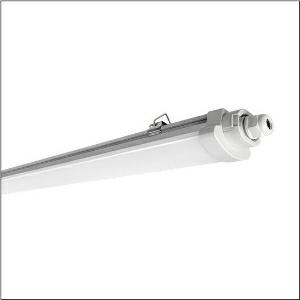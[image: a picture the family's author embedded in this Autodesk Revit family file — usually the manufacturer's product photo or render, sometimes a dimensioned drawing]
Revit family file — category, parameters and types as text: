
# Revit family: monsun_r__41_51fk20mn460a003_94ec
name_source: partatom
category: Lighting Fixtures
units: mm (PartAtom-declared; Revit-internal decimal feet)

## family parameters
Cut with Voids When Loaded = No
Host = Face
Light Source = No
Part Type = Normal
Room Calculation Point = No
Round Connector Dimension = Use Diameter
Shared = No

## types (1)
- --- (1 x LED, 6000 lm, 46 W, 4000K)
    Apparent Load = 46 VA
    CIE Flux Codes = 44 74 91 91 100
    Color Rendering = 80
    Color Temperature = 4000K
    Default Elevation = 1800 mm
    Description = Monsun® 41, damp-proof luminaire, primary optical cover: diffuser, of PC, frosted, light emission: direct distribution, primary light characteristic: symmetric, installation type: suspended mounting, surface-mounted, LED, rated luminous flux: 6.000lm, luminous efficacy: 130lm/W, light colour: 840, colour temperature: 4000K, control gear: ON/OFF Multilumen, with terminal, 3-pole, through-wiring: 3x 1.5mm², mains connection: 220..240V, AC, 50/60Hz, rated input power: 46W, housing, luminaire housing, of PC, grey, length: 1.500mm, width: 79mm, height: 52mm, end cap, of PC, grey, ceiling mounting element, of stainless steel (V2A), protection rating (complete): IP65, insulation class (complete): insulation class II (safety insulation), certification: CE, UKCA, protection symbol: D, impact resistance: IK08, permissible operating ambient temperature: -20..+35°C, corresponds to IFS (International Featured Standards) requirements for safety and quality in the food industry, contact your sales advisor before using the luminaires in applications with unclear chemical exposure, large temperature fluctuations or condensation-forming humidity, packaging unit: 1 piece
    Height = 54 mm
    Lamp = 1 x LED
    Lamp Light Flux = 6000 lm
    Lamp Power = 46 W
    Lamp count = 1
    Length = 1500 mm
    Luminous efficacy = 130 lm/W
    Manufacturer = Siteco
    ModVariant = No
    Model = 51FK20MN460A003
    Mounting Place = Ceiling
    Mounting Type = Surface mounted
    Number of Poles = 1
    OnlyDefault = Yes
    Power Factor = 1
    Product Name = Monsun® 41
    Product group = damp-proof luminaire
    ProductGroupID = 300
    Protection Class = Protection class II
    Protection Degree = IP 65
    RLX_Detail_Level = 1
    RLX_Emergency_Light_Flux = 0 lm
    RLX_Emergency_Type = 0
    RLX_Emergency_Type_DB = No
    RlxData = <blob elided: 28997 chars, md5=bc7abbda>
    Socket = socket
    Standby Power = 0 W
    System Light Flux = 6000 lm
    System Power = 46 W
    Type Comments = factory setting: luminous flux: 100 % | (HIGH)
    Type Image = l_1007037.jpg
    URL = http://relux.com
    VarID = @adj_174690
    Voltage = 0 V
    Weight = 0.00 kg
    Width = 79 mm

## geometry (parser evidence)
native form markers: Blend x4, Sweep x12
no freeform markers — native parametric forms only
